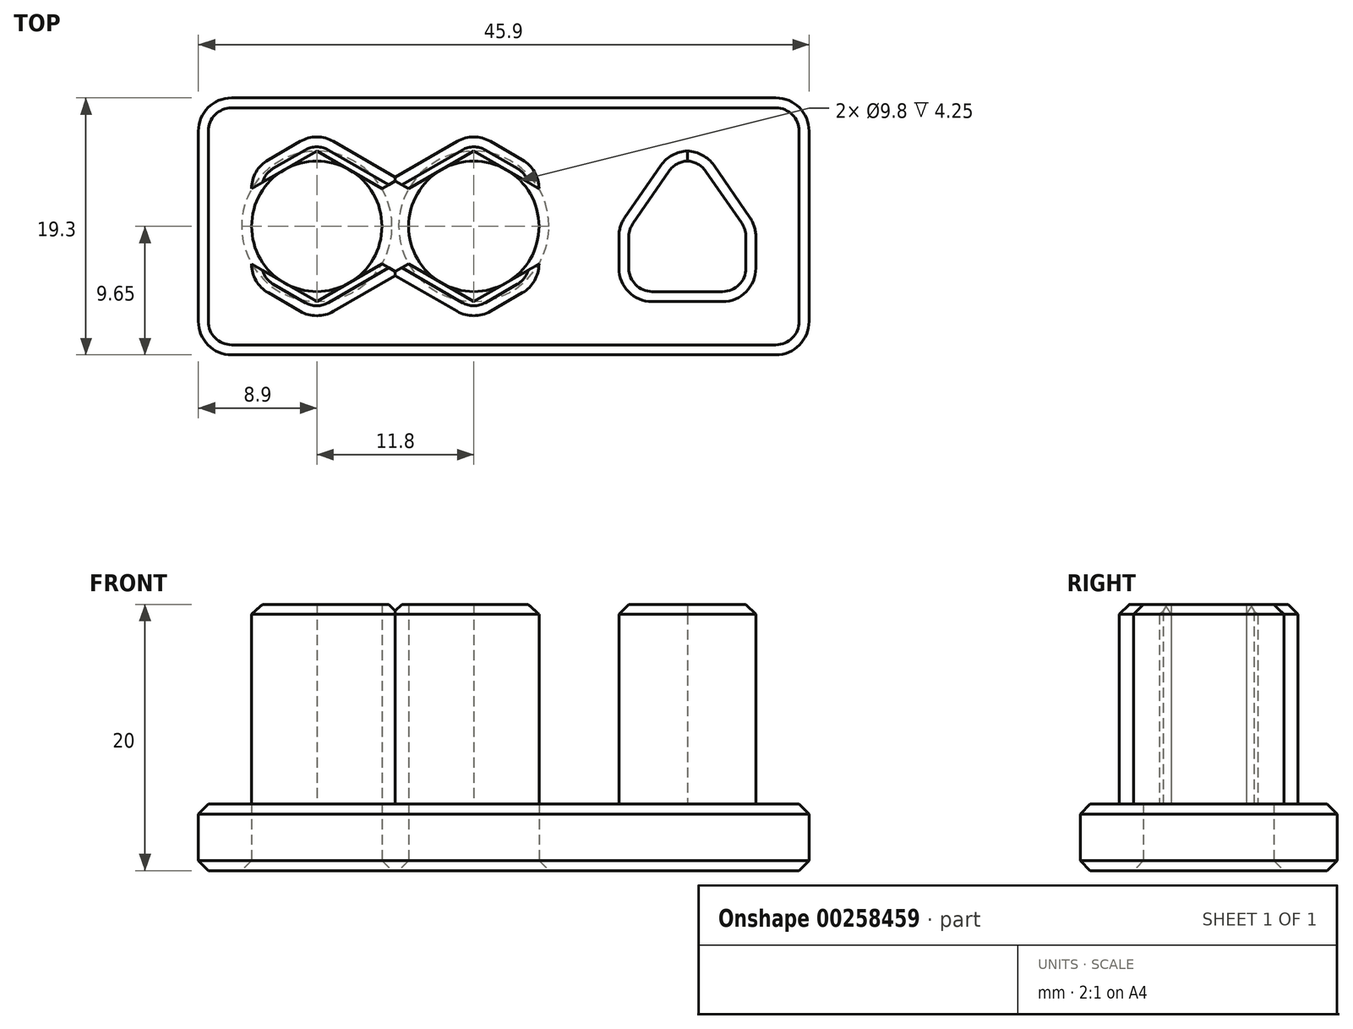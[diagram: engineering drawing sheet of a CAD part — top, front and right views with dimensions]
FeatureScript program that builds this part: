
annotation { "Feature Type Name" : "Feature", "Feature Type Description" : "" }
export const myFeature = defineFeature(function(context is Context, id is Id, definition is map)
    precondition{}
    {
        {
            var Q0;
            Q0=qCreatedBy(makeId("Top.planeOp"),FACE);
            var sketch = newSketch(context, id + "F0", { "sketchPlane" : qUnion([Q0])});
            skCircle(sketch, "E0", {"center": v(0, 0) * mm, "radius": 4.9 * mm});
            skLineSegment(sketch, "E1.bottom", {"start": v(14.8, 5.65) * mm, "end": v(17.3, 5.65) * mm});
            skPoint(sketch, "E1.middle", {"position": v(16.05, 0) * mm});
            skLineSegment(sketch, "E2.bottom", {"start": v(-20.7, 9.65) * mm, "end": v(25.2, 9.65) * mm});
            skLineSegment(sketch, "E2.top", {"start": v(-20.7, -9.65) * mm, "end": v(25.2, -9.65) * mm});
            skLineSegment(sketch, "E2.left", {"start": v(-20.7, 9.65) * mm, "end": v(-20.7, -9.65) * mm});
            skLineSegment(sketch, "E2.right", {"start": v(25.2, 9.65) * mm, "end": v(25.2, -9.65) * mm});
            skPoint(sketch, "E3", {"position": v(10.9, 0) * mm});
            skPoint(sketch, "E4", {"position": v(21.2, 0) * mm});
            skPoint(sketch, "E5.orphan", {"position": v(10.9, -5.65) * mm});
            skPoint(sketch, "E6.orphan", {"position": v(21.2, -5.65) * mm});
            skPoint(sketch, "E7", {"position": v(16.05, 5.65) * mm});
            skPoint(sketch, "E8", {"position": v(14.8, 5.65) * mm});
            skPoint(sketch, "E9", {"position": v(17.3, 5.65) * mm});
            skLineSegment(sketch, "E10", {"start": v(10.9, 0) * mm, "end": v(14.8, 5.65) * mm});
            skLineSegment(sketch, "E11", {"start": v(17.3, 5.65) * mm, "end": v(21.2, 0) * mm});
            skPoint(sketch, "E1.left.start.orphan", {"position": v(10.9, 5.65) * mm});
            skPoint(sketch, "E1.right.start.orphan", {"position": v(21.2, 5.65) * mm});
            skLineSegment(sketch, "E12", {"start": v(10.9, 0) * mm, "end": v(10.9, -5.65) * mm});
            skLineSegment(sketch, "E13", {"start": v(21.2, -5.65) * mm, "end": v(21.2, 0) * mm});
            skLineSegment(sketch, "E14", {"start": v(10.9, -5.65) * mm, "end": v(21.2, -5.65) * mm});
            skCircle(sketch, "E15", {"center": v(-11.8, 0) * mm, "radius": 4.9 * mm});
            skSolve(sketch);
        }
        {
            var Q0;
            Q0=makeQuery(id+"F0.imprint","IMPRINT",FACE,{"disambiguationData":[TD([[makeQuery(id+"F0.imprint","IMPRINT",EDGE,{"derivedFrom":sQuery(id+"F0.wireOp",EDGE,"E1.bottom")}),1.0]])]});
            var Q1;
            Q1=makeQuery(id+"F0.imprint","IMPRINT",FACE,{"disambiguationData":[TD([[makeQuery(id+"F0.imprint","IMPRINT",EDGE,{"derivedFrom":sQuery(id+"F0.wireOp",EDGE,"2ZkgInUv-5Nc7-WfQW-b4Kx-MGSRiltoAYJD")}),1.0]])]});
            var Q2;
            Q2=makeQuery(id+"F0.imprint","IMPRINT",FACE,{"disambiguationData":[TD([[makeQuery(id+"F0.imprint","IMPRINT",EDGE,{"derivedFrom":sQuery(id+"F0.wireOp",EDGE,"1SZ0JJ8j-nMDB-SVSY-mIdr-uC8MpVukoWS3")}),1.0]])]});
            var Q3;
            Q3=makeQuery(id+"F0.imprint","IMPRINT",FACE,{"disambiguationData":[TD([[makeQuery(id+"F0.imprint","IMPRINT",EDGE,{"derivedFrom":sQuery(id+"F0.wireOp",EDGE,"6UWYFoiz-xTeY-Ll6c-E06G-l3tQbFwgcraV")}),1.0]])]});
            var Q4;
            Q4=makeQuery(id+"F0.imprint","IMPRINT",FACE,{"disambiguationData":[TD([[makeQuery(id+"F0.imprint","IMPRINT",EDGE,{"derivedFrom":sQuery(id+"F0.wireOp",EDGE,"WCPchwxm-nEYR-rkoF-Yh02-TqD8vz6mbd4c")}),1.0]])]});
            var Q5;
            Q5=makeQuery(id+"F0.imprint","IMPRINT",FACE,{"disambiguationData":[TD([[makeQuery(id+"F0.imprint","IMPRINT",EDGE,{"derivedFrom":sQuery(id+"F0.wireOp",EDGE,"aakPY5ld-LYcw-7Zhq-pDX8-MrTg78qSgB2D")}),1.0]])]});
            var Q6;
            Q6=makeQuery(id+"F0.imprint","IMPRINT",FACE,{"disambiguationData":[TD([[makeQuery(id+"F0.imprint","IMPRINT",EDGE,{"derivedFrom":sQuery(id+"F0.wireOp",EDGE,"r2T5tCJW-hIjZ-mevY-SNhR-kN73oQGiL5mh")}),1.0]])]});
            var Q7;
            Q7=makeQuery(id+"F0.imprint","IMPRINT",FACE,{"disambiguationData":[TD([[makeQuery(id+"F0.imprint","IMPRINT",EDGE,{"derivedFrom":sQuery(id+"F0.wireOp",EDGE,"joK2IAnL-IShy-NAhP-NmX9-mCvCKGJXUlgC")}),1.0]])]});
            var Q8;
            Q8=makeQuery(id+"F0.imprint","IMPRINT",FACE,{"disambiguationData":[TD([[makeQuery(id+"F0.imprint","IMPRINT",EDGE,{"derivedFrom":sQuery(id+"F0.wireOp",EDGE,"Qra82nAW-1LtQ-fXKT-0feO-dY6BCh0kF5di")}),1.0]])]});
            var Q9;
            Q9=makeQuery(id+"F0.imprint","IMPRINT",FACE,{"disambiguationData":[TD([[makeQuery(id+"F0.imprint","IMPRINT",EDGE,{"derivedFrom":sQuery(id+"F0.wireOp",EDGE,"E1.bottom")}),-1.0]])]});
            extrude(context, id + "F1", {"entities" : qUnion([Q0, Q1, Q2, Q3, Q4, Q5, Q6, Q7, Q8, Q9]), "depth" : 5 * mm});
        }
        {
            var Q0;
            Q0=makeQuery(id+"F1.opExtrude","CAP_FACE",FACE,{"disambiguationData":[OSD([sQuery(id+"F0.wireOp",EDGE,"E0"),sQuery(id+"F0.wireOp",EDGE,"E2.bottom"),sQuery(id+"F0.wireOp",EDGE,"E2.top"),sQuery(id+"F0.wireOp",EDGE,"E2.left"),sQuery(id+"F0.wireOp",EDGE,"E2.right")])],"isStart":false});
            var sketch = newSketch(context, id + "F2", { "sketchPlane" : qUnion([Q0])});
            skLineSegment(sketch, "E16.8", {"start": v(10.9, 0) * mm, "end": v(14.8, 5.65) * mm});
            skLineSegment(sketch, "E16.9", {"start": v(14.8, 5.65) * mm, "end": v(17.3, 5.65) * mm});
            skLineSegment(sketch, "E16.10", {"start": v(17.3, 5.65) * mm, "end": v(21.2, 0) * mm});
            skLineSegment(sketch, "E16.11", {"start": v(21.2, -5.65) * mm, "end": v(21.2, 0) * mm});
            skLineSegment(sketch, "E16.12", {"start": v(10.9, -5.65) * mm, "end": v(21.2, -5.65) * mm});
            skLineSegment(sketch, "E16.13", {"start": v(10.9, 0) * mm, "end": v(10.9, -5.65) * mm});
            skCircle(sketch, "E17.0", {"center": v(0, 0) * mm, "radius": 4.9 * mm, "construction": true});
            skCircle(sketch, "E17.1", {"center": v(-11.8, 0) * mm, "radius": 4.9 * mm, "construction": true});
            skLineSegment(sketch, "E18.0", {"start": v(-6.9, 2.83) * mm, "end": v(-6.9, -2.83) * mm, "construction": true});
            skLineSegment(sketch, "E18.1", {"start": v(-6.9, -2.83) * mm, "end": v(-11.8, -5.66) * mm});
            skLineSegment(sketch, "E18.2", {"start": v(-11.8, -5.66) * mm, "end": v(-16.7, -2.83) * mm});
            skLineSegment(sketch, "E18.3", {"start": v(-16.7, -2.83) * mm, "end": v(-16.7, 2.83) * mm, "construction": true});
            skLineSegment(sketch, "E18.4", {"start": v(-16.7, 2.83) * mm, "end": v(-11.8, 5.66) * mm});
            skLineSegment(sketch, "E18.5", {"start": v(-11.8, 5.66) * mm, "end": v(-6.9, 2.83) * mm});
            skPoint(sketch, "E18.0.midPoint", {"position": v(-6.9, 0) * mm});
            skLineSegment(sketch, "E19.0", {"start": v(-4.9, -2.83) * mm, "end": v(-4.9, 2.83) * mm, "construction": true});
            skLineSegment(sketch, "E19.1", {"start": v(-4.9, 2.83) * mm, "end": v(0, 5.66) * mm});
            skLineSegment(sketch, "E19.2", {"start": v(0, 5.66) * mm, "end": v(4.9, 2.83) * mm});
            skLineSegment(sketch, "E19.3", {"start": v(4.9, 2.83) * mm, "end": v(4.9, -2.83) * mm, "construction": true});
            skLineSegment(sketch, "E19.4", {"start": v(4.9, -2.83) * mm, "end": v(0, -5.66) * mm});
            skLineSegment(sketch, "E19.5", {"start": v(0, -5.66) * mm, "end": v(-4.9, -2.83) * mm});
            skPoint(sketch, "E19.0.midPoint", {"position": v(-4.9, 0) * mm});
            skLineSegment(sketch, "E20.0", {"start": v(-11.8, 7.1) * mm, "end": v(-5.65, 3.55) * mm});
            skLineSegment(sketch, "E20.1", {"start": v(-5.65, -3.55) * mm, "end": v(-11.8, -7.1) * mm});
            skLineSegment(sketch, "E20.2", {"start": v(-11.8, -7.1) * mm, "end": v(-17.95, -3.55) * mm});
            skLineSegment(sketch, "E20.3", {"start": v(-5.65, 3.55) * mm, "end": v(-5.65, -3.55) * mm, "construction": true});
            skLineSegment(sketch, "E20.4", {"start": v(-17.95, -3.55) * mm, "end": v(-17.95, 3.55) * mm, "construction": true});
            skLineSegment(sketch, "E20.5", {"start": v(-17.95, 3.55) * mm, "end": v(-11.8, 7.1) * mm});
            skLineSegment(sketch, "E21.0", {"start": v(-6.15, -3.55) * mm, "end": v(-6.15, 3.55) * mm, "construction": true});
            skLineSegment(sketch, "E21.1", {"start": v(0, 7.1) * mm, "end": v(6.15, 3.55) * mm});
            skLineSegment(sketch, "E21.2", {"start": v(6.15, 3.55) * mm, "end": v(6.15, -3.55) * mm, "construction": true});
            skLineSegment(sketch, "E21.3", {"start": v(-6.15, 3.55) * mm, "end": v(0, 7.1) * mm});
            skLineSegment(sketch, "E21.4", {"start": v(6.15, -3.55) * mm, "end": v(0, -7.1) * mm});
            skLineSegment(sketch, "E21.5", {"start": v(0, -7.1) * mm, "end": v(-6.15, -3.55) * mm});
            skLineSegment(sketch, "E22", {"start": v(-17.95, 3.55) * mm, "end": v(-16.7, 2.83) * mm});
            skLineSegment(sketch, "E23", {"start": v(-17.95, -3.55) * mm, "end": v(-16.7, -2.83) * mm});
            skLineSegment(sketch, "E24", {"start": v(-6.9, -2.83) * mm, "end": v(-5.65, -3.55) * mm});
            skLineSegment(sketch, "E25", {"start": v(-6.9, 2.83) * mm, "end": v(-5.65, 3.55) * mm});
            skLineSegment(sketch, "E26", {"start": v(-6.15, 3.55) * mm, "end": v(-4.9, 2.83) * mm});
            skLineSegment(sketch, "E27", {"start": v(-6.15, -3.55) * mm, "end": v(-4.9, -2.83) * mm});
            skLineSegment(sketch, "E28", {"start": v(4.9, -2.83) * mm, "end": v(6.15, -3.55) * mm});
            skLineSegment(sketch, "E29", {"start": v(4.9, 2.83) * mm, "end": v(6.15, 3.55) * mm});
            skSolve(sketch);
        }
        {
            var Q0;
            Q0=makeQuery(id+"F2.imprint","IMPRINT",FACE,{"disambiguationData":[TD([[makeQuery(id+"F2.imprint","IMPRINT",EDGE,{"derivedFrom":sQuery(id+"F2.wireOp",EDGE,"339b621a-e242-4678-8d8c-c001c8a3955f.0")}),-1.0]])]});
            var Q1;
            Q1=makeQuery(id+"F2.imprint","IMPRINT",FACE,{"disambiguationData":[TD([[makeQuery(id+"F2.imprint","IMPRINT",EDGE,{"derivedFrom":sQuery(id+"F2.wireOp",EDGE,"E16.8")}),-1.0]])]});
            var Q2;
            Q2=makeQuery(id+"F2.imprint","IMPRINT",FACE,{"disambiguationData":[TD([[makeQuery(id+"F2.imprint","IMPRINT",EDGE,{"derivedFrom":sQuery(id+"F2.wireOp",EDGE,"339b621a-e242-4678-8d8c-c001c8a3955f.2")}),-1.0]])]});
            var Q3;
            Q3=makeQuery(id+"F2.imprint","IMPRINT",FACE,{"disambiguationData":[TD([[makeQuery(id+"F2.imprint","IMPRINT",EDGE,{"derivedFrom":sQuery(id+"F2.wireOp",EDGE,"E20.1")}),-1.0]])]});
            var Q4;
            Q4=makeQuery(id+"F2.imprint","IMPRINT",FACE,{"disambiguationData":[TD([[makeQuery(id+"F2.imprint","IMPRINT",EDGE,{"derivedFrom":sQuery(id+"F2.wireOp",EDGE,"E21.4")}),-1.0]])]});
            var Q5;
            Q5=makeQuery(id+"F2.imprint","IMPRINT",FACE,{"disambiguationData":[TD([[makeQuery(id+"F2.imprint","IMPRINT",EDGE,{"derivedFrom":sQuery(id+"F2.wireOp",EDGE,"E21.1")}),-1.0]])]});
            var Q6;
            Q6=makeQuery(id+"F2.imprint","IMPRINT",FACE,{"disambiguationData":[TD([[makeQuery(id+"F2.imprint","IMPRINT",EDGE,{"derivedFrom":sQuery(id+"F2.wireOp",EDGE,"E20.0")}),-1.0]])]});
            var Q7;
            {var subQ8=sQuery(id+"F2.wireOp",EDGE,"E20.5");Q7=makeQuery(id+"F2.imprint","IMPRINT",FACE,{"disambiguationData":[TD([[makeQuery(id+"F2.imprint","IMPRINT",EDGE,{"derivedFrom":subQ8}),-1.0]])]});}
            var Q8;
            {var subQ13=sQuery(id+"F2.wireOp",EDGE,"E20.2");Q8=makeQuery(id+"F2.imprint","IMPRINT",FACE,{"disambiguationData":[TD([[makeQuery(id+"F2.imprint","IMPRINT",EDGE,{"derivedFrom":subQ13}),-1.0]])]});}
            extrude(context, id + "F3", {"entities" : qUnion([Q0, Q1, Q2, Q3, Q4, Q5, Q6, Q7, Q8]), "operationType" : NewBodyOperationType.ADD, "depth" : 15 * mm});
        }
        {
            var Q0;
            Q0=makeQuery(id+"F1.opExtrude","SWEPT_EDGE",EDGE,{"disambiguationData":[OSD([sQuery(id+"F0.wireOp",EDGE,"E2.top"),sQuery(id+"F0.wireOp",EDGE,"E2.right")])]});
            var Q1;
            Q1=makeQuery(id+"F1.opExtrude","SWEPT_EDGE",EDGE,{"disambiguationData":[OSD([sQuery(id+"F0.wireOp",EDGE,"E2.bottom"),sQuery(id+"F0.wireOp",EDGE,"E2.right")])]});
            var Q2;
            Q2=makeQuery(id+"F1.opExtrude","SWEPT_EDGE",EDGE,{"disambiguationData":[OSD([sQuery(id+"F0.wireOp",EDGE,"E2.bottom"),sQuery(id+"F0.wireOp",EDGE,"E2.left")])]});
            var Q3;
            Q3=makeQuery(id+"F1.opExtrude","SWEPT_EDGE",EDGE,{"disambiguationData":[OSD([sQuery(id+"F0.wireOp",EDGE,"E2.top"),sQuery(id+"F0.wireOp",EDGE,"E2.left")])]});
            var Q4;
            Q4=makeQuery(id+"F3.opExtrude","SWEPT_EDGE",EDGE,{"disambiguationData":[OSD([sQuery(id+"F2.wireOp",EDGE,"E16.8"),sQuery(id+"F2.wireOp",EDGE,"E16.9")])]});
            var Q5;
            Q5=makeQuery(id+"F3.opExtrude","SWEPT_EDGE",EDGE,{"disambiguationData":[OSD([sQuery(id+"F2.wireOp",EDGE,"E16.9"),sQuery(id+"F2.wireOp",EDGE,"E16.10")])]});
            var Q6;
            Q6=makeQuery(id+"F3.opExtrude","SWEPT_EDGE",EDGE,{"disambiguationData":[OSD([sQuery(id+"F2.wireOp",EDGE,"E16.11"),sQuery(id+"F2.wireOp",EDGE,"E16.12")])]});
            var Q7;
            Q7=makeQuery(id+"F3.opExtrude","SWEPT_EDGE",EDGE,{"disambiguationData":[OSD([sQuery(id+"F2.wireOp",EDGE,"E16.12"),sQuery(id+"F2.wireOp",EDGE,"E16.13")])]});
            var Q8;
            Q8=makeQuery(id+"F3.opExtrude","SWEPT_EDGE",EDGE,{"disambiguationData":[OSD([sQuery(id+"F2.wireOp",EDGE,"E16.10"),sQuery(id+"F2.wireOp",EDGE,"E16.11")])]});
            var Q9;
            Q9=makeQuery(id+"F3.opExtrude","SWEPT_EDGE",EDGE,{"disambiguationData":[OSD([sQuery(id+"F2.wireOp",EDGE,"E16.8"),sQuery(id+"F2.wireOp",EDGE,"E16.13")])]});
            var Q10;
            Q10=makeQuery(id+"F3.opExtrude","SWEPT_EDGE",EDGE,{"disambiguationData":[OSD([sQuery(id+"F2.wireOp",EDGE,"E21.4"),sQuery(id+"F2.wireOp",EDGE,"E21.5")])]});
            var Q11;
            Q11=makeQuery(id+"F3.opExtrude","SWEPT_EDGE",EDGE,{"disambiguationData":[OSD([sQuery(id+"F2.wireOp",EDGE,"E20.1"),sQuery(id+"F2.wireOp",EDGE,"E20.2")])]});
            var Q12;
            Q12=makeQuery(id+"F3.opExtrude","SWEPT_EDGE",EDGE,{"disambiguationData":[OSD([sQuery(id+"F2.wireOp",EDGE,"E21.1"),sQuery(id+"F2.wireOp",EDGE,"E21.3")])]});
            var Q13;
            Q13=makeQuery(id+"F3.opExtrude","SWEPT_EDGE",EDGE,{"disambiguationData":[OSD([sQuery(id+"F2.wireOp",EDGE,"E20.0"),sQuery(id+"F2.wireOp",EDGE,"E20.5")])]});
            var Q14;
            Q14=makeQuery(id+"F3.opExtrude","SWEPT_EDGE",EDGE,{"disambiguationData":[OSD([sQuery(id+"F2.wireOp",EDGE,"E21.1"),sQuery(id+"F2.wireOp",EDGE,"E29")])]});
            var Q15;
            Q15=makeQuery(id+"F3.opExtrude","SWEPT_EDGE",EDGE,{"disambiguationData":[OSD([sQuery(id+"F2.wireOp",EDGE,"E21.4"),sQuery(id+"F2.wireOp",EDGE,"E28")])]});
            var Q16;
            Q16=makeQuery(id+"F3.opExtrude","SWEPT_EDGE",EDGE,{"disambiguationData":[OSD([sQuery(id+"F2.wireOp",EDGE,"E20.2"),sQuery(id+"F2.wireOp",EDGE,"E23")])]});
            var Q17;
            Q17=makeQuery(id+"F3.opExtrude","SWEPT_EDGE",EDGE,{"disambiguationData":[OSD([sQuery(id+"F2.wireOp",EDGE,"E20.5"),sQuery(id+"F2.wireOp",EDGE,"E22")])]});
            fillet(context, id + "F4", {"entities" : qUnion([Q0, Q1, Q2, Q3, Q4, Q5, Q6, Q7, Q8, Q9, Q10, Q11, Q12, Q13, Q14, Q15, Q16, Q17]), "radius" : 2.5 * mm, "tangentPropagation" : true, "allowEdgeOverflow" : false});
        }
        {
            var Q0;
            Q0=makeQuery(id+"F3.opExtrude","CAP_FACE",FACE,{"disambiguationData":[OSD([sQuery(id+"F2.wireOp",EDGE,"E16.8"),sQuery(id+"F2.wireOp",EDGE,"E16.9"),sQuery(id+"F2.wireOp",EDGE,"E16.10"),sQuery(id+"F2.wireOp",EDGE,"E16.11"),sQuery(id+"F2.wireOp",EDGE,"E16.12"),sQuery(id+"F2.wireOp",EDGE,"E16.13")])],"isStart":false});
            var Q1;
            Q1=makeQuery(id+"F3.opExtrude","CAP_FACE",FACE,{"disambiguationData":[OSD([sQuery(id+"F2.wireOp",EDGE,"3c6c1ebe-9b8c-48d7-aa0e-6f1b34b6b162.0"),sQuery(id+"F2.wireOp",EDGE,"3c6c1ebe-9b8c-48d7-aa0e-6f1b34b6b162.1"),sQuery(id+"F2.wireOp",EDGE,"3c6c1ebe-9b8c-48d7-aa0e-6f1b34b6b162.2"),sQuery(id+"F2.wireOp",EDGE,"3c6c1ebe-9b8c-48d7-aa0e-6f1b34b6b162.3"),sQuery(id+"F2.wireOp",EDGE,"3c6c1ebe-9b8c-48d7-aa0e-6f1b34b6b162.4"),sQuery(id+"F2.wireOp",EDGE,"3c6c1ebe-9b8c-48d7-aa0e-6f1b34b6b162.5"),sQuery(id+"F2.wireOp",EDGE,"339b621a-e242-4678-8d8c-c001c8a3955f.0"),sQuery(id+"F2.wireOp",EDGE,"339b621a-e242-4678-8d8c-c001c8a3955f.1"),sQuery(id+"F2.wireOp",EDGE,"339b621a-e242-4678-8d8c-c001c8a3955f.2"),sQuery(id+"F2.wireOp",EDGE,"339b621a-e242-4678-8d8c-c001c8a3955f.3"),sQuery(id+"F2.wireOp",EDGE,"339b621a-e242-4678-8d8c-c001c8a3955f.4"),sQuery(id+"F2.wireOp",EDGE,"339b621a-e242-4678-8d8c-c001c8a3955f.5")])],"isStart":false});
            var Q2;
            Q2=makeQuery(id+"F1.opExtrude","CAP_EDGE",EDGE,{"disambiguationData":[OSD([sQuery(id+"F0.wireOp",EDGE,"E2.top")])],"isStart":false});
            var Q3;
            Q3=makeQuery(id+"F1.opExtrude","CAP_FACE",FACE,{"disambiguationData":[OSD([sQuery(id+"F0.wireOp",EDGE,"E0"),sQuery(id+"F0.wireOp",EDGE,"E2.bottom"),sQuery(id+"F0.wireOp",EDGE,"E2.top"),sQuery(id+"F0.wireOp",EDGE,"E2.left"),sQuery(id+"F0.wireOp",EDGE,"E2.right")])],"isStart":true});
            var Q4;
            Q4=makeQuery(id+"F3.opExtrude","CAP_EDGE",EDGE,{"disambiguationData":[OSD([sQuery(id+"F2.wireOp",EDGE,"E21.4")])],"isStart":false});
            var Q5;
            Q5=makeQuery(id+"F3.opExtrude","CAP_EDGE",EDGE,{"disambiguationData":[OSD([sQuery(id+"F2.wireOp",EDGE,"E20.1")])],"isStart":false});
            var Q6;
            Q6=makeQuery(id+"F3.opExtrude","CAP_EDGE",EDGE,{"disambiguationData":[OSD([sQuery(id+"F2.wireOp",EDGE,"E21.1")])],"isStart":false});
            var Q7;
            {var subQ0=sQuery(id+"F2.wireOp",EDGE,"E20.5");var subQ1=sQuery(id+"F2.wireOp",EDGE,"E20.0");Q7=makeQuery(id+"F4.opFillet","BLEND_EDGE",EDGE,{"blendedFrom":[makeQuery(id+"F3.opExtrude","SWEPT_EDGE",EDGE,{"disambiguationData":[OSD([subQ1,subQ0])]}),makeQuery(id+"F3.opExtrude","CAP_FACE",FACE,{"disambiguationData":[OSD([sQuery(id+"F2.wireOp",EDGE,"E18.4"),sQuery(id+"F2.wireOp",EDGE,"E18.5"),sQuery(id+"F2.wireOp",EDGE,"E19.1"),sQuery(id+"F2.wireOp",EDGE,"E19.2"),subQ1,subQ0,sQuery(id+"F2.wireOp",EDGE,"E21.1"),sQuery(id+"F2.wireOp",EDGE,"E21.3"),sQuery(id+"F2.wireOp",EDGE,"E22"),sQuery(id+"F2.wireOp",EDGE,"E25"),sQuery(id+"F2.wireOp",EDGE,"E26"),sQuery(id+"F2.wireOp",EDGE,"E29")])],"isStart":false})],"blendedInto":[makeQuery(id+"F3.opExtrude","CAP_FACE",FACE,{"disambiguationData":[OSD([sQuery(id+"F2.wireOp",EDGE,"E18.4"),sQuery(id+"F2.wireOp",EDGE,"E18.5"),sQuery(id+"F2.wireOp",EDGE,"E19.1"),sQuery(id+"F2.wireOp",EDGE,"E19.2"),subQ1,subQ0,sQuery(id+"F2.wireOp",EDGE,"E21.1"),sQuery(id+"F2.wireOp",EDGE,"E21.3"),sQuery(id+"F2.wireOp",EDGE,"E22"),sQuery(id+"F2.wireOp",EDGE,"E25"),sQuery(id+"F2.wireOp",EDGE,"E26"),sQuery(id+"F2.wireOp",EDGE,"E29")])],"isStart":false})]});}
            chamfer(context, id + "F5", {"entities" : qUnion([Q0, Q1, Q2, Q3, Q4, Q5, Q6, Q7]), "width" : .75 * mm, "tangentPropagation" : true});
        }
    });
